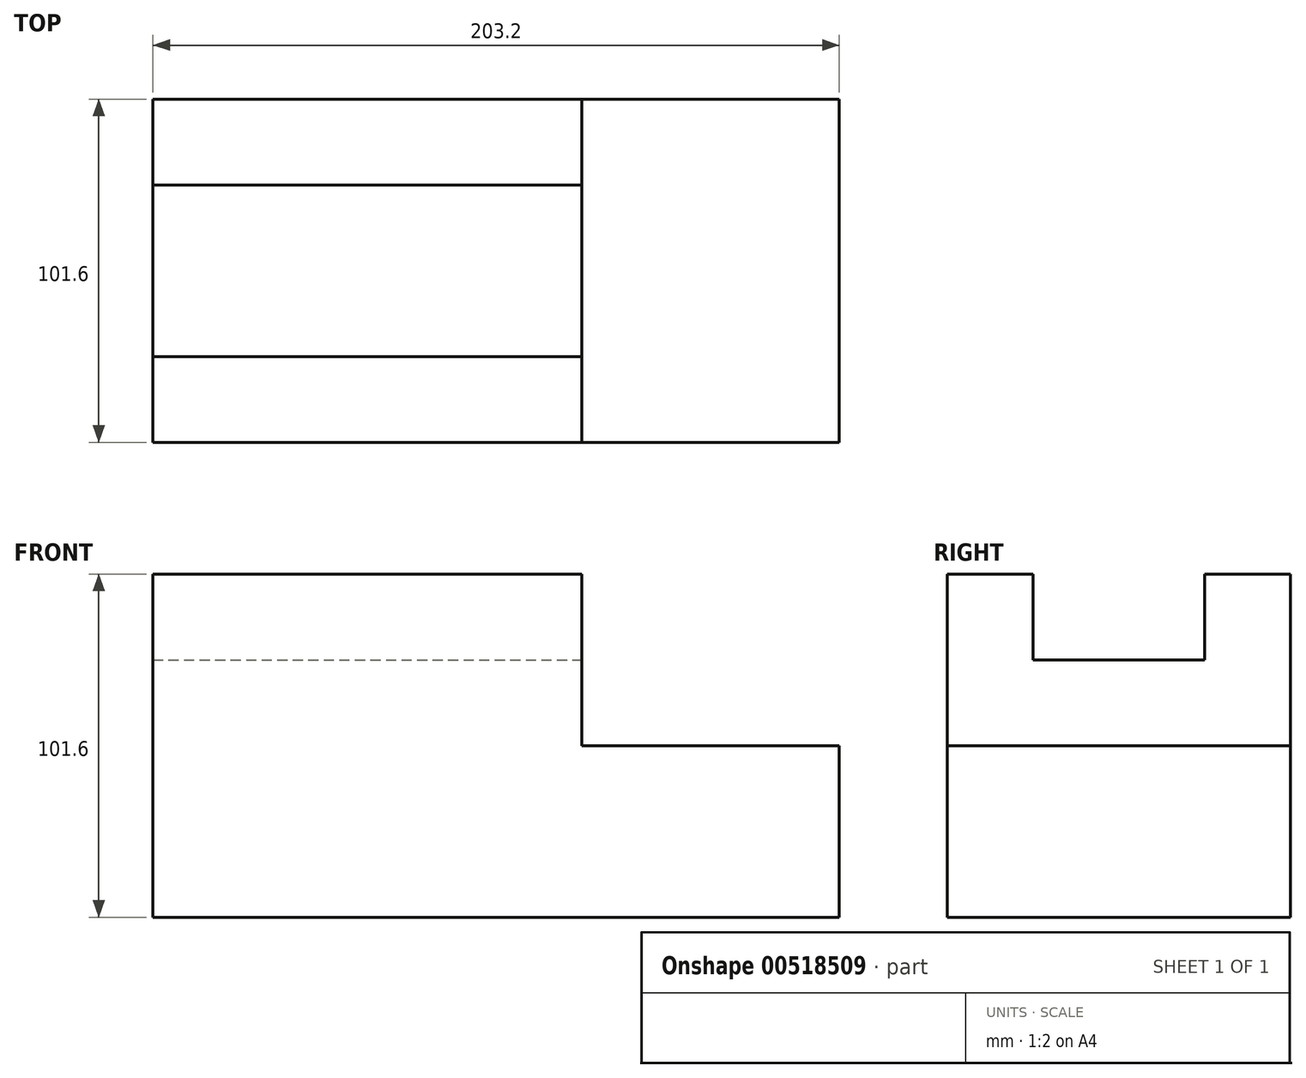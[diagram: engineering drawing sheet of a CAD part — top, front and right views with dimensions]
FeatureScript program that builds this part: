
annotation { "Feature Type Name" : "Feature", "Feature Type Description" : "" }
export const myFeature = defineFeature(function(context is Context, id is Id, definition is map)
    precondition{}
    {
        {
            var Q0;
            Q0=qCreatedBy(makeId("Front.planeOp"),FACE);
            var sketch = newSketch(context, id + "F0", { "sketchPlane" : qUnion([Q0])});
            skLineSegment(sketch, "E0.bottom", {"start": v(-137.13, -79.33) * mm, "end": v(66.07, -79.33) * mm});
            skLineSegment(sketch, "E0.top", {"start": v(-137.13, 22.27) * mm, "end": v(66.07, 22.27) * mm});
            skLineSegment(sketch, "E0.left", {"start": v(-137.13, -79.33) * mm, "end": v(-137.13, 22.27) * mm});
            skLineSegment(sketch, "E0.right", {"start": v(66.07, -79.33) * mm, "end": v(66.07, 22.27) * mm});
            skSolve(sketch);
        }
        {
            var Q0;
            Q0=qSketchRegion(id+"F0",true);
            extrude(context, id + "F1", {"entities" : qUnion([Q0]), "depth" : 101.6 * mm});
        }
        {
            var Q0;
            Q0=makeQuery(id+"F1.opExtrude","SWEPT_FACE",FACE,{"disambiguationData":[OSD([sQuery(id+"F0.wireOp",EDGE,"E0.top")])]});
            var sketch = newSketch(context, id + "F2", { "sketchPlane" : qUnion([Q0])});
            skLineSegment(sketch, "E1.bottom", {"start": v(66.07, -101.6) * mm, "end": v(-10.13, -101.6) * mm});
            skLineSegment(sketch, "E1.top", {"start": v(66.07, 0) * mm, "end": v(-10.13, 0) * mm});
            skLineSegment(sketch, "E1.left", {"start": v(66.07, -101.6) * mm, "end": v(66.07, 0) * mm});
            skLineSegment(sketch, "E1.right", {"start": v(-10.13, -101.6) * mm, "end": v(-10.13, 0) * mm});
            skSolve(sketch);
        }
        {
            var Q0;
            Q0=qSketchRegion(id+"F2",true);
            extrude(context, id + "F3", {"entities" : qUnion([Q0]), "operationType" : NewBodyOperationType.REMOVE, "oppositeDirection" : true, "depth" : 50.8 * mm});
        }
        {
            var Q0;
            Q0=makeQuery(id+"F1.opExtrude","SWEPT_FACE",FACE,{"disambiguationData":[OSD([sQuery(id+"F0.wireOp",EDGE,"E0.top")])]});
            var sketch = newSketch(context, id + "F4", { "sketchPlane" : qUnion([Q0])});
            skLineSegment(sketch, "E2.bottom", {"start": v(-137.13, -25.4) * mm, "end": v(-10.13, -25.4) * mm});
            skLineSegment(sketch, "E2.top", {"start": v(-137.13, -76.2) * mm, "end": v(-10.13, -76.2) * mm});
            skLineSegment(sketch, "E2.left", {"start": v(-137.13, -25.4) * mm, "end": v(-137.13, -76.2) * mm});
            skLineSegment(sketch, "E2.right", {"start": v(-10.13, -25.4) * mm, "end": v(-10.13, -76.2) * mm});
            skSolve(sketch);
        }
        {
            var Q0;
            Q0=qSketchRegion(id+"F4",true);
            extrude(context, id + "F5", {"entities" : qUnion([Q0]), "operationType" : NewBodyOperationType.REMOVE, "oppositeDirection" : true, "depth" : 25.4 * mm});
        }
    });
